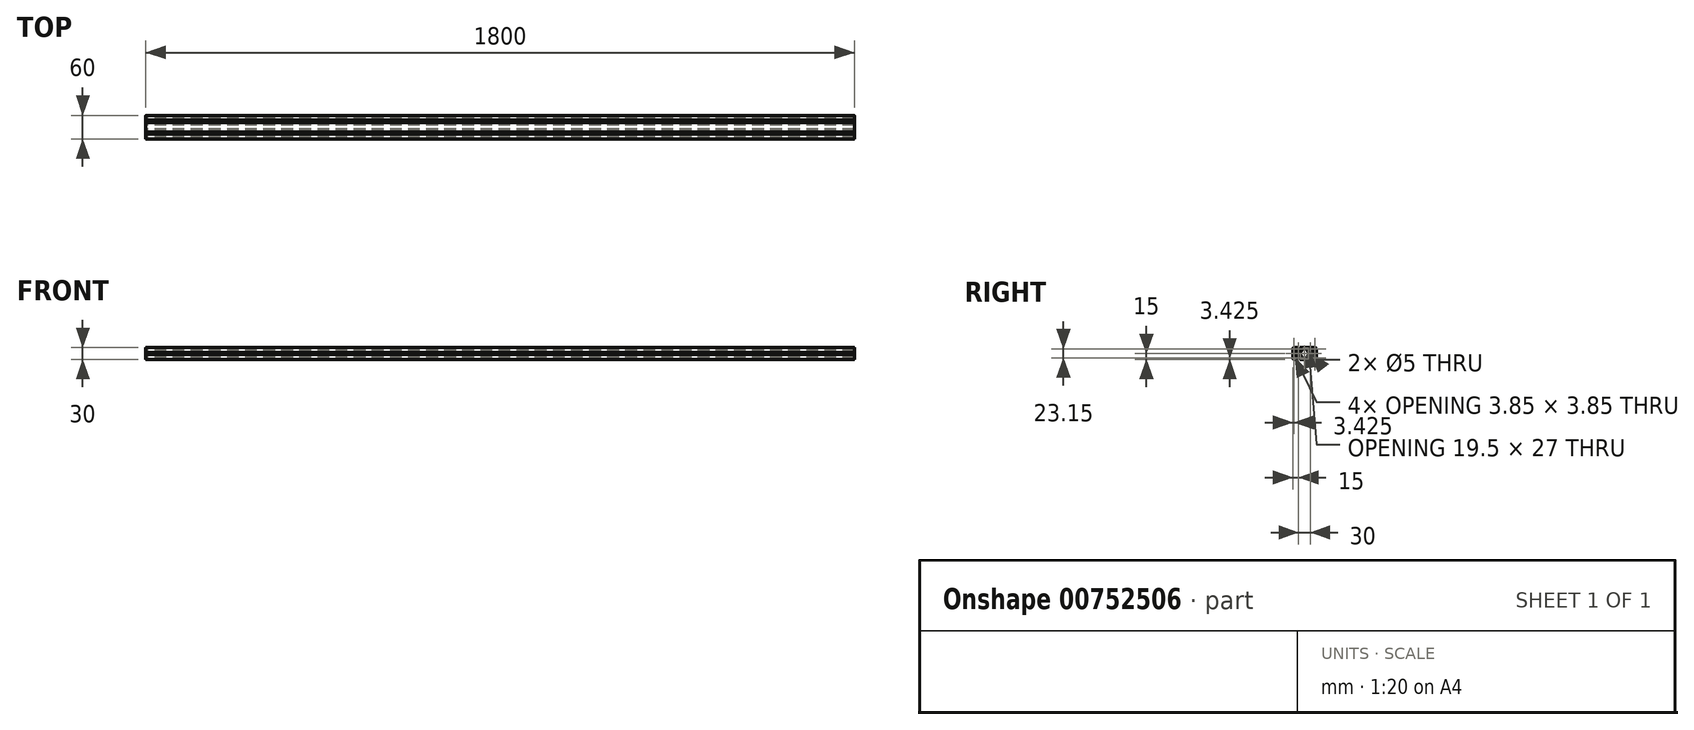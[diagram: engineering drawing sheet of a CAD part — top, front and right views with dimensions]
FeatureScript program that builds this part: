
annotation { "Feature Type Name" : "Feature", "Feature Type Description" : "" }
export const myFeature = defineFeature(function(context is Context, id is Id, definition is map)
    precondition{}
    {
        {
            var Q0;
            Q0=qCreatedBy(makeId("Right.planeOp"),FACE);
            var sketch = newSketch(context, id + "F0", { "sketchPlane" : qUnion([Q0])});
            skLineSegment(sketch, "E0.bottom", {"start": v(-12, 15) * mm, "end": v(-3.1, 15) * mm});
            skLineSegment(sketch, "E0.top", {"start": v(-12, -15) * mm, "end": v(-3.1, -15) * mm});
            skLineSegment(sketch, "E1", {"start": v(0, 31.7) * mm, "end": v(0, -24.01) * mm, "construction": true});
            skLineSegment(sketch, "E2", {"start": v(-29.71, 0) * mm, "end": v(21.95, 0) * mm, "construction": true});
            skLineSegment(sketch, "E3", {"start": v(-3.1, 15) * mm, "end": v(-3.1, 12.8) * mm});
            skLineSegment(sketch, "E4", {"start": v(-3.9, 12) * mm, "end": v(-5.6, 12) * mm});
            skLineSegment(sketch, "E5", {"start": v(-5.6, 12) * mm, "end": v(-5.6, 13.5) * mm});
            skLineSegment(sketch, "E6", {"start": v(-5.6, 13.5) * mm, "end": v(-8.15, 13.5) * mm});
            skLineSegment(sketch, "E7", {"start": v(-8.15, 13.5) * mm, "end": v(-8.15, 10.8) * mm});
            skLineSegment(sketch, "E8", {"start": v(-7.27, 8.68) * mm, "end": v(-4.72, 6.13) * mm});
            skLineSegment(sketch, "E9", {"start": v(-2.6, 5.25) * mm, "end": v(2.6, 5.25) * mm});
            skLineSegment(sketch, "E10", {"start": v(4.72, 6.13) * mm, "end": v(7.27, 8.68) * mm});
            skLineSegment(sketch, "E11", {"start": v(8.15, 10.8) * mm, "end": v(8.15, 13.5) * mm});
            skLineSegment(sketch, "E12", {"start": v(8.15, 13.5) * mm, "end": v(5.6, 13.5) * mm});
            skLineSegment(sketch, "E13", {"start": v(5.6, 13.5) * mm, "end": v(5.6, 12) * mm});
            skLineSegment(sketch, "E14", {"start": v(5.6, 12) * mm, "end": v(3.9, 12) * mm});
            skLineSegment(sketch, "E15", {"start": v(3.1, 12.8) * mm, "end": v(3.1, 15) * mm});
            skLineSegment(sketch, "E16.trimOffspring", {"start": v(3.1, 15) * mm, "end": v(12, 15) * mm});
            skLineSegment(sketch, "E17.bottom", {"start": v(-12, 13.5) * mm, "end": v(-9.65, 13.5) * mm});
            skLineSegment(sketch, "E17.top", {"start": v(-13.5, 9.65) * mm, "end": v(-9.65, 9.65) * mm});
            skLineSegment(sketch, "E17.left", {"start": v(-13.5, 12) * mm, "end": v(-13.5, 9.65) * mm});
            skLineSegment(sketch, "E17.right", {"start": v(-9.65, 13.5) * mm, "end": v(-9.65, 9.65) * mm});
            skPoint(sketch, "E18.visualSharp", {"position": v(-13.5, 13.5) * mm});
            skArc(sketch, "E18.filletArc", {"start": v(-12, 13.5) * mm, "mid": v(-13.06, 13.06) * mm, "end": v(-13.5, 12) * mm});
            skPoint(sketch, "E19.visualSharp", {"position": v(-14.85, 15) * mm});
            skArc(sketch, "E19.filletArc", {"start": v(-12, 15) * mm, "mid": v(-14.12, 14.12) * mm, "end": v(-15, 12) * mm});
            skPoint(sketch, "E20.visualSharp", {"position": v(-14.85, -15) * mm});
            skArc(sketch, "E20.filletArc", {"start": v(-15, -12) * mm, "mid": v(-14.12, -14.12) * mm, "end": v(-12, -15) * mm});
            skPoint(sketch, "E21.visualSharp", {"position": v(15.15, -15) * mm});
            skPoint(sketch, "E22.visualSharp", {"position": v(-8.15, 9.56) * mm});
            skArc(sketch, "E22.filletArc", {"start": v(-8.15, 10.8) * mm, "mid": v(-7.92, 9.66) * mm, "end": v(-7.27, 8.68) * mm});
            skPoint(sketch, "E23.visualSharp", {"position": v(-3.84, 5.25) * mm});
            skArc(sketch, "E23.filletArc", {"start": v(-4.72, 6.13) * mm, "mid": v(-3.74, 5.48) * mm, "end": v(-2.6, 5.25) * mm});
            skPoint(sketch, "E24.visualSharp", {"position": v(3.84, 5.25) * mm});
            skArc(sketch, "E24.filletArc", {"start": v(2.6, 5.25) * mm, "mid": v(3.74, 5.48) * mm, "end": v(4.72, 6.13) * mm});
            skPoint(sketch, "E25.visualSharp", {"position": v(8.15, 9.56) * mm});
            skArc(sketch, "E25.filletArc", {"start": v(7.27, 8.68) * mm, "mid": v(7.92, 9.66) * mm, "end": v(8.15, 10.8) * mm});
            skPoint(sketch, "E26.visualSharp", {"position": v(3.1, 12) * mm});
            skArc(sketch, "E26.filletArc", {"start": v(3.1, 12.8) * mm, "mid": v(3.33, 12.23) * mm, "end": v(3.9, 12) * mm});
            skPoint(sketch, "E27.visualSharp", {"position": v(-3.1, 12) * mm});
            skArc(sketch, "E27.filletArc", {"start": v(-3.9, 12) * mm, "mid": v(-3.33, 12.23) * mm, "end": v(-3.1, 12.8) * mm});
            skLineSegment(sketch, "E28.1.0", {"start": v(-5.25, -2.6) * mm, "end": v(-5.25, 2.6) * mm});
            skLineSegment(sketch, "E28.1.1", {"start": v(-12.8, 3.1) * mm, "end": v(-15, 3.1) * mm});
            skLineSegment(sketch, "E28.1.2", {"start": v(-6.13, 4.72) * mm, "end": v(-8.68, 7.27) * mm});
            skPoint(sketch, "E28.1.3", {"position": v(-12, -3.1) * mm});
            skLineSegment(sketch, "E28.1.4", {"start": v(-13.5, -5.6) * mm, "end": v(-13.5, -8.15) * mm});
            skPoint(sketch, "E28.1.5", {"position": v(-5.25, 3.84) * mm});
            skLineSegment(sketch, "E28.1.6", {"start": v(-13.5, -12) * mm, "end": v(-13.5, -9.65) * mm});
            skPoint(sketch, "E28.1.7", {"position": v(-5.25, -3.84) * mm});
            skLineSegment(sketch, "E28.1.8", {"start": v(-10.8, 8.15) * mm, "end": v(-13.5, 8.15) * mm});
            skLineSegment(sketch, "E28.1.9", {"start": v(-9.65, -13.5) * mm, "end": v(-9.65, -9.65) * mm});
            skLineSegment(sketch, "E28.1.10", {"start": v(-12, -13.5) * mm, "end": v(-9.65, -13.5) * mm});
            skLineSegment(sketch, "E28.1.11", {"start": v(-13.5, -8.15) * mm, "end": v(-10.8, -8.15) * mm});
            skLineSegment(sketch, "E28.1.12", {"start": v(-13.5, -9.65) * mm, "end": v(-9.65, -9.65) * mm});
            skPoint(sketch, "E28.1.13", {"position": v(-9.56, 8.15) * mm});
            skLineSegment(sketch, "E28.1.14", {"start": v(-8.68, -7.27) * mm, "end": v(-6.13, -4.72) * mm});
            skPoint(sketch, "E28.1.15", {"position": v(-12, 3.1) * mm});
            skPoint(sketch, "E28.1.16", {"position": v(-9.56, -8.15) * mm});
            skLineSegment(sketch, "E28.1.17", {"start": v(-15, -3.1) * mm, "end": v(-12.8, -3.1) * mm});
            skLineSegment(sketch, "E28.1.18", {"start": v(-13.5, 8.15) * mm, "end": v(-13.5, 5.6) * mm});
            skArc(sketch, "E28.1.19", {"start": v(-10.8, -8.15) * mm, "mid": v(-9.66, -7.92) * mm, "end": v(-8.68, -7.27) * mm});
            skArc(sketch, "E28.1.20", {"start": v(-6.13, -4.72) * mm, "mid": v(-5.48, -3.74) * mm, "end": v(-5.25, -2.6) * mm});
            skArc(sketch, "E28.1.21", {"start": v(-13.5, -12) * mm, "mid": v(-13.06, -13.06) * mm, "end": v(-12, -13.5) * mm});
            skArc(sketch, "E28.1.22", {"start": v(-8.68, 7.27) * mm, "mid": v(-9.66, 7.92) * mm, "end": v(-10.8, 8.15) * mm});
            skArc(sketch, "E28.1.23", {"start": v(-5.25, 2.6) * mm, "mid": v(-5.48, 3.74) * mm, "end": v(-6.13, 4.72) * mm});
            skLineSegment(sketch, "E28.1.24", {"start": v(-12, -5.6) * mm, "end": v(-13.5, -5.6) * mm});
            skLineSegment(sketch, "E28.1.25", {"start": v(-13.5, 5.6) * mm, "end": v(-12, 5.6) * mm});
            skLineSegment(sketch, "E28.1.26", {"start": v(-12, 5.6) * mm, "end": v(-12, 3.9) * mm});
            skLineSegment(sketch, "E28.1.27", {"start": v(-12, -3.9) * mm, "end": v(-12, -5.6) * mm});
            skArc(sketch, "E28.1.28", {"start": v(-12, -3.9) * mm, "mid": v(-12.23, -3.33) * mm, "end": v(-12.8, -3.1) * mm});
            skArc(sketch, "E28.1.29", {"start": v(-12.8, 3.1) * mm, "mid": v(-12.23, 3.33) * mm, "end": v(-12, 3.9) * mm});
            skLineSegment(sketch, "E28.2.0", {"start": v(2.6, -5.25) * mm, "end": v(-2.6, -5.25) * mm});
            skLineSegment(sketch, "E28.2.1", {"start": v(-3.1, -12.8) * mm, "end": v(-3.1, -15) * mm});
            skLineSegment(sketch, "E28.2.2", {"start": v(-4.72, -6.13) * mm, "end": v(-7.27, -8.68) * mm});
            skPoint(sketch, "E28.2.3", {"position": v(3.1, -12) * mm});
            skLineSegment(sketch, "E28.2.4", {"start": v(5.6, -13.5) * mm, "end": v(8.15, -13.5) * mm});
            skPoint(sketch, "E28.2.5", {"position": v(-3.84, -5.25) * mm});
            skPoint(sketch, "E28.2.7", {"position": v(3.84, -5.25) * mm});
            skLineSegment(sketch, "E28.2.8", {"start": v(-8.15, -10.8) * mm, "end": v(-8.15, -13.5) * mm});
            skLineSegment(sketch, "E28.2.11", {"start": v(8.15, -13.5) * mm, "end": v(8.15, -10.8) * mm});
            skLineSegment(sketch, "E28.2.12", {"start": v(9.65, -13.5) * mm, "end": v(9.65, -9.65) * mm});
            skPoint(sketch, "E28.2.13", {"position": v(-8.15, -9.56) * mm});
            skLineSegment(sketch, "E28.2.14", {"start": v(7.27, -8.68) * mm, "end": v(4.72, -6.13) * mm});
            skPoint(sketch, "E28.2.15", {"position": v(-3.1, -12) * mm});
            skPoint(sketch, "E28.2.16", {"position": v(8.15, -9.56) * mm});
            skLineSegment(sketch, "E28.2.17", {"start": v(3.1, -15) * mm, "end": v(3.1, -12.8) * mm});
            skLineSegment(sketch, "E28.2.18", {"start": v(-8.15, -13.5) * mm, "end": v(-5.6, -13.5) * mm});
            skArc(sketch, "E28.2.19", {"start": v(8.15, -10.8) * mm, "mid": v(7.92, -9.66) * mm, "end": v(7.27, -8.68) * mm});
            skArc(sketch, "E28.2.20", {"start": v(4.72, -6.13) * mm, "mid": v(3.74, -5.48) * mm, "end": v(2.6, -5.25) * mm});
            skArc(sketch, "E28.2.22", {"start": v(-7.27, -8.68) * mm, "mid": v(-7.92, -9.66) * mm, "end": v(-8.15, -10.8) * mm});
            skArc(sketch, "E28.2.23", {"start": v(-2.6, -5.25) * mm, "mid": v(-3.74, -5.48) * mm, "end": v(-4.72, -6.13) * mm});
            skLineSegment(sketch, "E28.2.24", {"start": v(5.6, -12) * mm, "end": v(5.6, -13.5) * mm});
            skLineSegment(sketch, "E28.2.25", {"start": v(-5.6, -13.5) * mm, "end": v(-5.6, -12) * mm});
            skLineSegment(sketch, "E28.2.26", {"start": v(-5.6, -12) * mm, "end": v(-3.9, -12) * mm});
            skLineSegment(sketch, "E28.2.27", {"start": v(3.9, -12) * mm, "end": v(5.6, -12) * mm});
            skArc(sketch, "E28.2.28", {"start": v(3.9, -12) * mm, "mid": v(3.33, -12.23) * mm, "end": v(3.1, -12.8) * mm});
            skArc(sketch, "E28.2.29", {"start": v(-3.1, -12.8) * mm, "mid": v(-3.33, -12.23) * mm, "end": v(-3.9, -12) * mm});
            skLineSegment(sketch, "E28.3.0", {"start": v(5.25, 2.6) * mm, "end": v(5.25, -2.6) * mm});
            skLineSegment(sketch, "E28.3.2", {"start": v(6.13, -4.72) * mm, "end": v(8.68, -7.27) * mm});
            skPoint(sketch, "E28.3.5", {"position": v(5.25, -3.84) * mm});
            skPoint(sketch, "E28.3.7", {"position": v(5.25, 3.84) * mm});
            skLineSegment(sketch, "E28.3.9", {"start": v(9.65, 13.5) * mm, "end": v(9.65, 9.56) * mm});
            skPoint(sketch, "E28.3.13", {"position": v(9.56, -8.15) * mm});
            skLineSegment(sketch, "E28.3.14", {"start": v(8.71, 7.3) * mm, "end": v(6.13, 4.72) * mm});
            skPoint(sketch, "E28.3.16", {"position": v(9.56, 8.15) * mm});
            skArc(sketch, "E28.3.20", {"start": v(6.13, 4.72) * mm, "mid": v(5.48, 3.74) * mm, "end": v(5.25, 2.6) * mm});
            skArc(sketch, "E28.3.23", {"start": v(5.25, -2.6) * mm, "mid": v(5.48, -3.74) * mm, "end": v(6.13, -4.72) * mm});
            skPoint(sketch, "E28.center", {"position": v(0, 0) * mm});
            skLineSegment(sketch, "E29.trimOffspring", {"start": v(-15, -3.1) * mm, "end": v(-15, -12) * mm});
            skLineSegment(sketch, "E30.trimOffspring", {"start": v(3.1, -15) * mm, "end": v(12, -15) * mm});
            skLineSegment(sketch, "E31", {"start": v(-15, 12) * mm, "end": v(-15, 3.1) * mm});
            skCircle(sketch, "E32", {"center": v(0, 0) * mm, "radius": 2.5 * mm});
            skPoint(sketch, "E33.1.0.0", {"position": v(26.9, -12) * mm});
            skPoint(sketch, "E33.1.0.1", {"position": v(45.65, 15) * mm});
            skPoint(sketch, "E33.1.0.3", {"position": v(30, 0) * mm});
            skPoint(sketch, "E33.1.0.4", {"position": v(35.25, -3.84) * mm});
            skPoint(sketch, "E33.1.0.5", {"position": v(33.1, 12) * mm});
            skPoint(sketch, "E33.1.0.7", {"position": v(35.25, 3.84) * mm});
            skPoint(sketch, "E33.1.0.8", {"position": v(42, 3.1) * mm});
            skPoint(sketch, "E33.1.0.9", {"position": v(33.1, -12) * mm});
            skLineSegment(sketch, "E33.1.0.10", {"start": v(30, 31.7) * mm, "end": v(30, -24.01) * mm, "construction": true});
            skLineSegment(sketch, "E33.1.0.11", {"start": v(0.29, 0) * mm, "end": v(51.95, 0) * mm, "construction": true});
            skPoint(sketch, "E33.1.0.13", {"position": v(42.5, -2.6) * mm});
            skPoint(sketch, "E33.1.0.15", {"position": v(45.15, -15) * mm});
            skPoint(sketch, "E33.1.0.16", {"position": v(24.75, 3.84) * mm});
            skPoint(sketch, "E33.1.0.17", {"position": v(24.75, -3.84) * mm});
            skPoint(sketch, "E33.1.0.18", {"position": v(26.16, 5.25) * mm});
            skLineSegment(sketch, "E33.1.0.20", {"start": v(32.6, -5.25) * mm, "end": v(27.4, -5.25) * mm});
            skArc(sketch, "E33.1.0.21", {"start": v(42, -15) * mm, "mid": v(44.12, -14.12) * mm, "end": v(45, -12) * mm});
            skPoint(sketch, "E33.1.0.22", {"position": v(33.84, 5.25) * mm});
            skArc(sketch, "E33.1.0.23", {"start": v(45, 12) * mm, "mid": v(44.12, 14.12) * mm, "end": v(42, 15) * mm});
            skCircle(sketch, "E33.1.0.24", {"center": v(30, 0) * mm, "radius": 2.5 * mm});
            skLineSegment(sketch, "E33.1.0.26", {"start": v(27.4, 5.25) * mm, "end": v(32.6, 5.25) * mm});
            skPoint(sketch, "E33.1.0.27", {"position": v(26.16, -5.25) * mm});
            skPoint(sketch, "E33.1.0.28", {"position": v(33.84, -5.25) * mm});
            skLineSegment(sketch, "E33.1.0.29", {"start": v(35.25, 2.6) * mm, "end": v(35.25, -2.6) * mm});
            skLineSegment(sketch, "E33.1.0.30", {"start": v(24.75, -2.6) * mm, "end": v(24.75, 2.6) * mm});
            skLineSegment(sketch, "E33.1.0.31", {"start": v(42.85, -3.1) * mm, "end": v(45, -3.1) * mm});
            skArc(sketch, "E33.1.0.32", {"start": v(24.75, 2.6) * mm, "mid": v(24.52, 3.74) * mm, "end": v(23.87, 4.72) * mm});
            skArc(sketch, "E33.1.0.34", {"start": v(35.25, -2.6) * mm, "mid": v(35.48, -3.74) * mm, "end": v(36.13, -4.72) * mm});
            skPoint(sketch, "E33.1.0.35", {"position": v(38.15, -9.56) * mm});
            skLineSegment(sketch, "E33.1.0.36", {"start": v(36.13, -4.72) * mm, "end": v(38.68, -7.27) * mm});
            skLineSegment(sketch, "E33.1.0.37", {"start": v(37.27, -8.68) * mm, "end": v(34.72, -6.13) * mm});
            skLineSegment(sketch, "E33.1.0.39", {"start": v(23.87, 4.72) * mm, "end": v(21.32, 7.27) * mm});
            skPoint(sketch, "E33.1.0.40", {"position": v(20.44, 8.15) * mm});
            skLineSegment(sketch, "E33.1.0.41", {"start": v(33.1, -15) * mm, "end": v(33.1, -12.8) * mm});
            skLineSegment(sketch, "E33.1.0.43", {"start": v(43.5, -5.6) * mm, "end": v(42.05, -5.6) * mm});
            skPoint(sketch, "E33.1.0.44", {"position": v(21.85, 9.56) * mm});
            skLineSegment(sketch, "E33.1.0.45", {"start": v(21.85, -13.5) * mm, "end": v(24.4, -13.5) * mm});
            skLineSegment(sketch, "E33.1.0.46", {"start": v(42.05, -5.6) * mm, "end": v(42.05, -3.9) * mm});
            skPoint(sketch, "E33.1.0.47", {"position": v(20.44, -8.15) * mm});
            skArc(sketch, "E33.1.0.52", {"start": v(42.85, -3.1) * mm, "mid": v(42.29, -3.33) * mm, "end": v(42.05, -3.9) * mm});
            skLineSegment(sketch, "E33.1.0.54", {"start": v(26.9, -12.8) * mm, "end": v(26.9, -15) * mm});
            skLineSegment(sketch, "E33.1.0.55", {"start": v(45, -3.1) * mm, "end": v(45, -12) * mm});
            skArc(sketch, "E33.1.0.56", {"start": v(27.4, -5.25) * mm, "mid": v(26.26, -5.48) * mm, "end": v(25.28, -6.13) * mm});
            skLineSegment(sketch, "E33.1.0.57", {"start": v(24.4, -13.5) * mm, "end": v(24.4, -12) * mm});
            skArc(sketch, "E33.1.0.59", {"start": v(25.28, 6.13) * mm, "mid": v(26.26, 5.48) * mm, "end": v(27.4, 5.25) * mm});
            skLineSegment(sketch, "E33.1.0.61", {"start": v(25.28, -6.13) * mm, "end": v(22.73, -8.68) * mm});
            skLineSegment(sketch, "E33.1.0.62", {"start": v(21.32, -7.27) * mm, "end": v(23.87, -4.72) * mm});
            skLineSegment(sketch, "E33.1.0.63", {"start": v(33.1, -15) * mm, "end": v(42, -15) * mm});
            skLineSegment(sketch, "E33.1.0.64", {"start": v(24.4, -12) * mm, "end": v(26.1, -12) * mm});
            skArc(sketch, "E33.1.0.65", {"start": v(32.6, 5.25) * mm, "mid": v(33.74, 5.48) * mm, "end": v(34.72, 6.13) * mm});
            skLineSegment(sketch, "E33.1.0.66", {"start": v(43.5, -8.15) * mm, "end": v(43.5, -5.6) * mm});
            skPoint(sketch, "E33.1.0.67", {"position": v(38.15, 9.56) * mm});
            skPoint(sketch, "E33.1.0.68", {"position": v(39.56, -8.15) * mm});
            skLineSegment(sketch, "E33.1.0.69", {"start": v(21.85, -10.8) * mm, "end": v(21.85, -13.5) * mm});
            skLineSegment(sketch, "E33.1.0.70", {"start": v(18, -15) * mm, "end": v(26.9, -15) * mm});
            skLineSegment(sketch, "E33.1.0.71", {"start": v(45, 12) * mm, "end": v(45, 3.1) * mm});
            skLineSegment(sketch, "E33.1.0.72", {"start": v(22.73, 8.68) * mm, "end": v(25.28, 6.13) * mm});
            skArc(sketch, "E33.1.0.73", {"start": v(36.13, 4.72) * mm, "mid": v(35.48, 3.74) * mm, "end": v(35.25, 2.6) * mm});
            skPoint(sketch, "E33.1.0.74", {"position": v(26.9, 12) * mm});
            skArc(sketch, "E33.1.0.75", {"start": v(33.9, -12) * mm, "mid": v(33.33, -12.23) * mm, "end": v(33.1, -12.8) * mm});
            skArc(sketch, "E33.1.0.76", {"start": v(23.87, -4.72) * mm, "mid": v(24.52, -3.74) * mm, "end": v(24.75, -2.6) * mm});
            skPoint(sketch, "E33.1.0.77", {"position": v(39.56, 8.15) * mm});
            skArc(sketch, "E33.1.0.78", {"start": v(26.9, -12.8) * mm, "mid": v(26.67, -12.23) * mm, "end": v(26.1, -12) * mm});
            skPoint(sketch, "E33.1.0.79", {"position": v(21.85, -9.56) * mm});
            skLineSegment(sketch, "E33.1.0.80", {"start": v(33.1, 15) * mm, "end": v(42, 15) * mm});
            skLineSegment(sketch, "E33.1.0.82", {"start": v(39.65, -13.5) * mm, "end": v(39.65, -9.65) * mm});
            skLineSegment(sketch, "E33.1.0.84", {"start": v(42, 5.6) * mm, "end": v(43.5, 5.6) * mm});
            skLineSegment(sketch, "E33.1.0.85", {"start": v(43.5, 5.6) * mm, "end": v(43.5, 8.15) * mm});
            skLineSegment(sketch, "E33.1.0.87", {"start": v(20.35, 13.5) * mm, "end": v(20.35, 9.65) * mm});
            skLineSegment(sketch, "E33.1.0.88", {"start": v(43.5, 12) * mm, "end": v(43.5, 9.65) * mm});
            skLineSegment(sketch, "E33.1.0.93", {"start": v(42, 3.9) * mm, "end": v(42, 5.6) * mm});
            skLineSegment(sketch, "E33.1.0.94", {"start": v(40.8, -8.15) * mm, "end": v(43.5, -8.15) * mm});
            skArc(sketch, "E33.1.0.95", {"start": v(38.15, -10.8) * mm, "mid": v(37.92, -9.66) * mm, "end": v(37.27, -8.68) * mm});
            skLineSegment(sketch, "E33.1.0.96", {"start": v(20.35, -13.5) * mm, "end": v(20.35, -9.65) * mm});
            skArc(sketch, "E33.1.0.97", {"start": v(42, 3.9) * mm, "mid": v(42.23, 3.33) * mm, "end": v(42.8, 3.1) * mm});
            skLineSegment(sketch, "E33.1.0.98", {"start": v(39.65, 13.5) * mm, "end": v(39.65, 9.65) * mm});
            skArc(sketch, "E33.1.0.99", {"start": v(34.72, -6.13) * mm, "mid": v(33.74, -5.48) * mm, "end": v(32.6, -5.25) * mm});
            skLineSegment(sketch, "E33.1.0.101", {"start": v(42, 13.5) * mm, "end": v(39.65, 13.5) * mm});
            skArc(sketch, "E33.1.0.102", {"start": v(42, -13.5) * mm, "mid": v(43.06, -13.06) * mm, "end": v(43.5, -12) * mm});
            skLineSegment(sketch, "E33.1.0.104", {"start": v(43.5, 8.15) * mm, "end": v(40.76, 8.15) * mm});
            skArc(sketch, "E33.1.0.105", {"start": v(22.73, -8.68) * mm, "mid": v(22.08, -9.66) * mm, "end": v(21.85, -10.8) * mm});
            skLineSegment(sketch, "E33.1.0.107", {"start": v(43.5, 9.65) * mm, "end": v(39.65, 9.65) * mm});
            skLineSegment(sketch, "E33.1.0.108", {"start": v(35.6, -13.5) * mm, "end": v(38.15, -13.5) * mm});
            skLineSegment(sketch, "E33.1.0.109", {"start": v(45, 3.1) * mm, "end": v(42.8, 3.1) * mm});
            skArc(sketch, "E33.1.0.110", {"start": v(21.85, 10.8) * mm, "mid": v(22.08, 9.66) * mm, "end": v(22.73, 8.68) * mm});
            skLineSegment(sketch, "E33.1.0.111", {"start": v(38.68, 7.27) * mm, "end": v(36.13, 4.72) * mm});
            skLineSegment(sketch, "E33.1.0.112", {"start": v(35.6, -12) * mm, "end": v(35.6, -13.5) * mm});
            skLineSegment(sketch, "E33.1.0.113", {"start": v(42, -13.5) * mm, "end": v(39.65, -13.5) * mm});
            skLineSegment(sketch, "E33.1.0.115", {"start": v(33.9, -12) * mm, "end": v(35.6, -12) * mm});
            skArc(sketch, "E33.1.0.117", {"start": v(37.27, 8.68) * mm, "mid": v(37.92, 9.66) * mm, "end": v(38.15, 10.8) * mm});
            skArc(sketch, "E33.1.0.118", {"start": v(40.76, 8.15) * mm, "mid": v(39.64, 7.91) * mm, "end": v(38.68, 7.27) * mm});
            skLineSegment(sketch, "E33.1.0.119", {"start": v(38.15, 10.8) * mm, "end": v(38.15, 13.5) * mm});
            skLineSegment(sketch, "E33.1.0.120", {"start": v(38.15, 13.5) * mm, "end": v(35.6, 13.5) * mm});
            skLineSegment(sketch, "E33.1.0.121", {"start": v(35.6, 13.5) * mm, "end": v(35.6, 12) * mm});
            skLineSegment(sketch, "E33.1.0.122", {"start": v(18, 15) * mm, "end": v(26.9, 15) * mm});
            skLineSegment(sketch, "E33.1.0.123", {"start": v(26.9, 15) * mm, "end": v(26.9, 12.8) * mm});
            skLineSegment(sketch, "E33.1.0.124", {"start": v(24.4, 12) * mm, "end": v(24.4, 13.5) * mm});
            skLineSegment(sketch, "E33.1.0.125", {"start": v(24.4, 13.5) * mm, "end": v(21.85, 13.5) * mm});
            skLineSegment(sketch, "E33.1.0.126", {"start": v(21.85, 13.5) * mm, "end": v(21.85, 10.8) * mm});
            skLineSegment(sketch, "E33.1.0.127", {"start": v(34.72, 6.13) * mm, "end": v(37.27, 8.68) * mm});
            skLineSegment(sketch, "E33.1.0.128", {"start": v(35.6, 12) * mm, "end": v(33.9, 12) * mm});
            skLineSegment(sketch, "E33.1.0.129", {"start": v(43.5, -9.65) * mm, "end": v(39.65, -9.65) * mm});
            skLineSegment(sketch, "E33.1.0.130", {"start": v(33.1, 12.8) * mm, "end": v(33.1, 15) * mm});
            skLineSegment(sketch, "E33.1.0.131", {"start": v(43.5, -12) * mm, "end": v(43.5, -9.65) * mm});
            skArc(sketch, "E33.1.0.133", {"start": v(43.5, 12) * mm, "mid": v(43.06, 13.06) * mm, "end": v(42, 13.5) * mm});
            skLineSegment(sketch, "E33.1.0.134", {"start": v(38.15, -13.5) * mm, "end": v(38.15, -10.8) * mm});
            skArc(sketch, "E33.1.0.136", {"start": v(38.68, -7.27) * mm, "mid": v(39.66, -7.92) * mm, "end": v(40.8, -8.15) * mm});
            skLineSegment(sketch, "E33.1.0.138", {"start": v(26.1, 12) * mm, "end": v(24.4, 12) * mm});
            skArc(sketch, "E33.1.0.139", {"start": v(33.1, 12.8) * mm, "mid": v(33.33, 12.23) * mm, "end": v(33.9, 12) * mm});
            skArc(sketch, "E33.1.0.140", {"start": v(26.1, 12) * mm, "mid": v(26.67, 12.23) * mm, "end": v(26.9, 12.8) * mm});
            skLineSegment(sketch, "E33.direction1", {"start": v(-14.85, -15) * mm, "end": v(15.15, -15) * mm, "construction": true});
            skLineSegment(sketch, "E34", {"start": v(9.65, 13.5) * mm, "end": v(20.35, 13.5) * mm});
            skArc(sketch, "E35", {"start": v(8.71, 7.3) * mm, "mid": v(9.4, 8.34) * mm, "end": v(9.65, 9.56) * mm});
            skArc(sketch, "E36", {"start": v(20.35, 9.65) * mm, "mid": v(20.6, 8.37) * mm, "end": v(21.32, 7.27) * mm});
            skArc(sketch, "E37", {"start": v(9.65, -9.65) * mm, "mid": v(9.4, -8.36) * mm, "end": v(8.68, -7.27) * mm});
            skArc(sketch, "E38", {"start": v(21.32, -7.27) * mm, "mid": v(20.6, -8.37) * mm, "end": v(20.35, -9.65) * mm});
            skLineSegment(sketch, "E39", {"start": v(12, -15) * mm, "end": v(18, -15) * mm});
            skLineSegment(sketch, "E40", {"start": v(12, 15) * mm, "end": v(18.49, 15) * mm});
            skLineSegment(sketch, "E41", {"start": v(9.65, -13.5) * mm, "end": v(20.35, -13.5) * mm});
            skSolve(sketch);
        }
        {
            var Q0;
            Q0=qSketchRegion(id+"F0",true);
            extrude(context, id + "F1", {"entities" : qUnion([Q0]), "depth" : 1800 * mm, "offsetDistance" : 25 * mm});
        }
    });
